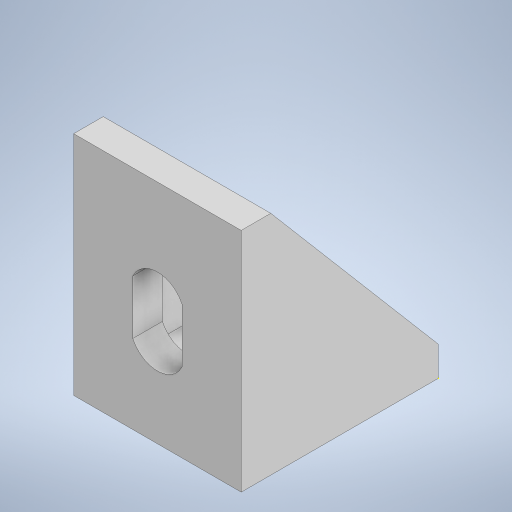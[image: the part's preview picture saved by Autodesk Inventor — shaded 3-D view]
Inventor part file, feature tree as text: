
AUTODESK INVENTOR PART (.ipt)
format: ipt  version: 2023.5 (Build 275446000, 446)  size: 251,392 bytes
history: native  units: in
note: dims shown in document units (in); Inventor stores cm internally (conversion verified against a paired STEP export)
features: sketch x7, extrude x6
ambient origin geometry x8: Origin, YZ Plane, XZ Plane, XY Plane, X Axis, Y Axis, Z Axis, Center Point
bodies: Solid1 (feature_tree)
feature tree (13):
  extrude  "Extrusion1"  Depth=0.6693in
  sketch  "Sketch2"  dims[d2=0.7874in d3=0.0in d4=0.1181in]
  extrude  "Extrusion2"  Depth=0.1181in
  extrude  "Extrusion3"  Depth=0.0945in TaperAngle=0.0deg
  extrude  "Extrusion4"  Depth=0.0945in
  extrude  "Extrusion5"  Depth=0.0945in TaperAngle=0.0deg
  sketch  "Sketch1"  dims[d0=0.1181in d1=0.6693in]
  sketch  "Sketch3"  dims[d5=0.7874in d6=0.0in d7=0.0945in d8=0.0in]
  sketch  "Sketch4"  dims[d9=0.0945in d10=0.0in d11=0.3346in]
  sketch  "Sketch5"  dims[d20=0.0945in d21=0.0in d23=0.0in d24=0.0945in]
  sketch  "Sketch6"  dims[d25=0.3346in]
  sketch  "Sketch7"
  extrude  "Extrusion6"  [1 undecoded]
note: 1 required parameter value undecoded (feature->parameter linkage not recoverable at this tier; creation-order binding heuristic only, values carry confidence <= 0.55)
